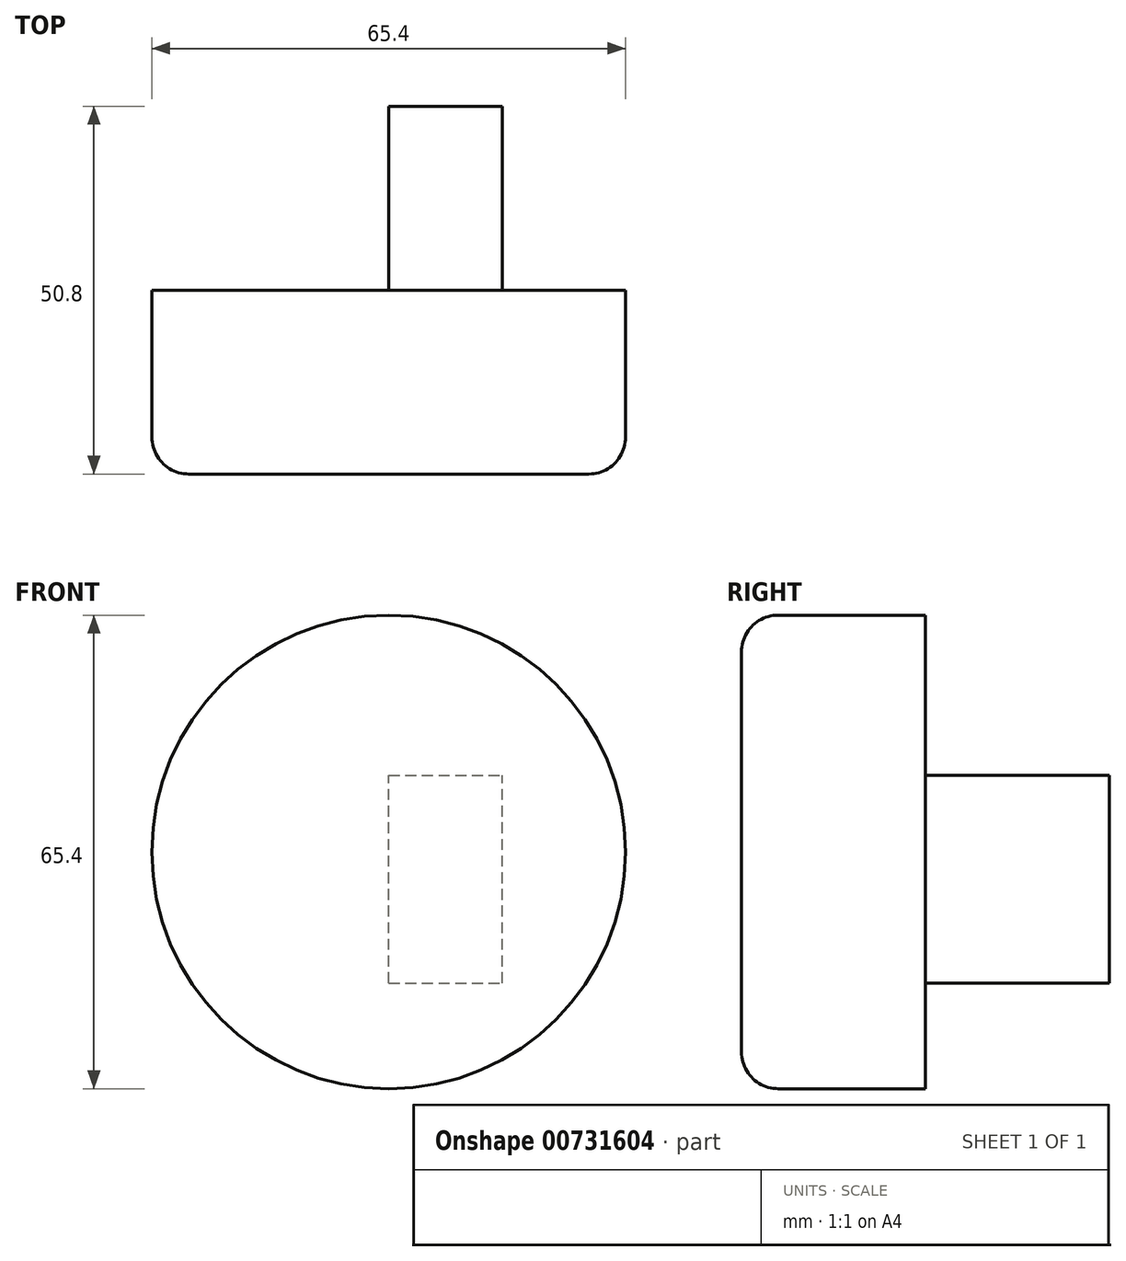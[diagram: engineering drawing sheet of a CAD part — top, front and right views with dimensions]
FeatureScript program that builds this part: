
annotation { "Feature Type Name" : "Feature", "Feature Type Description" : "" }
export const myFeature = defineFeature(function(context is Context, id is Id, definition is map)
    precondition{}
    {
        {
            var Q0;
            Q0=qCreatedBy(makeId("Front.planeOp"),FACE);
            var sketch = newSketch(context, id + "F0", { "sketchPlane" : qUnion([Q0])});
            skCircle(sketch, "E0", {"center": v(0, 0) * mm, "radius": 32.7 * mm});
            skSolve(sketch);
        }
        {
            var Q0;
            Q0=makeQuery(id+"F0.imprint","IMPRINT",FACE,{"disambiguationData":[TD([[makeQuery(id+"F0.imprint","IMPRINT",EDGE,{"derivedFrom":sQuery(id+"F0.wireOp",EDGE,"E0")}),1.0]])]});
            extrude(context, id + "F1", {"entities" : qUnion([Q0]), "depth" : 25.4 * mm, "offsetDistance" : 25.4 * mm});
        }
        {
            var Q0;
            Q0=makeQuery(id+"F1.opExtrude","CAP_EDGE",EDGE,{"disambiguationData":[OSD([sQuery(id+"F0.wireOp",EDGE,"E0")])],"isStart":false});
            fillet(context, id + "F2", {"entities" : qUnion([Q0]), "radius" : 5.08 * mm, "tangentPropagation" : true, "allowEdgeOverflow" : false});
        }
        {
            var Q0;
            Q0=makeQuery(id+"F1.opExtrude","CAP_FACE",FACE,{"disambiguationData":[OSD([sQuery(id+"F0.wireOp",EDGE,"E0")])],"isStart":true});
            var sketch = newSketch(context, id + "F3", { "sketchPlane" : qUnion([Q0])});
            skLineSegment(sketch, "E1.bottom", {"start": v(0, -18.11) * mm, "end": v(-15.7, -18.11) * mm});
            skLineSegment(sketch, "E1.top", {"start": v(0, 10.59) * mm, "end": v(-15.7, 10.59) * mm});
            skLineSegment(sketch, "E1.left", {"start": v(0, -18.11) * mm, "end": v(0, 10.59) * mm});
            skLineSegment(sketch, "E1.right", {"start": v(-15.7, -18.11) * mm, "end": v(-15.7, 10.59) * mm});
            skSolve(sketch);
        }
        {
            var Q0;
            Q0=makeQuery(id+"F3.imprint","IMPRINT",FACE,{"disambiguationData":[TD([[makeQuery(id+"F3.imprint","IMPRINT",EDGE,{"derivedFrom":sQuery(id+"F3.wireOp",EDGE,"E1.bottom")}),-1.0]])]});
            extrude(context, id + "F4", {"entities" : qUnion([Q0]), "operationType" : NewBodyOperationType.ADD, "depth" : 25.4 * mm, "offsetDistance" : 25.4 * mm});
        }
    });
